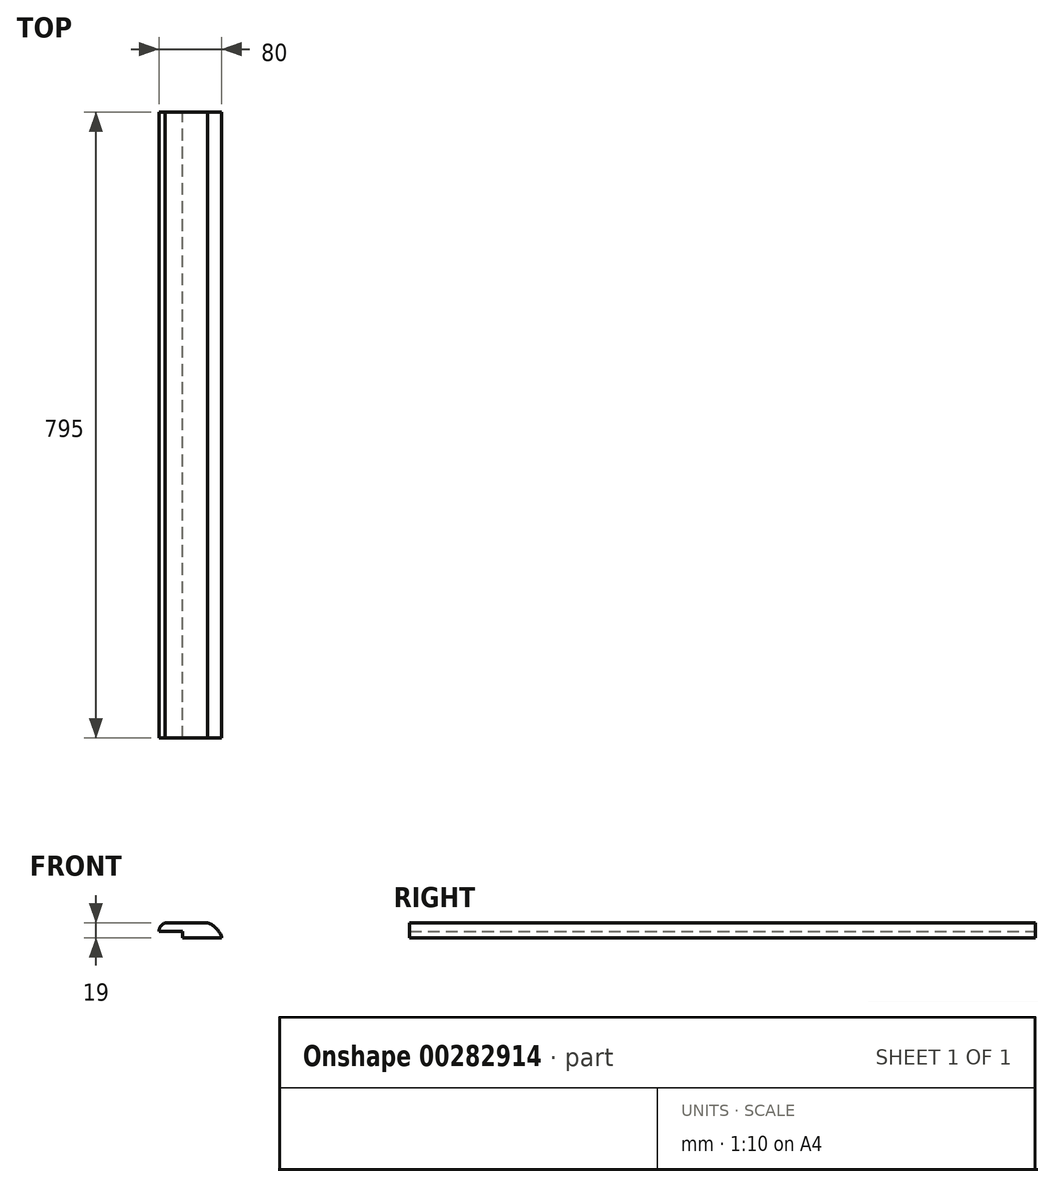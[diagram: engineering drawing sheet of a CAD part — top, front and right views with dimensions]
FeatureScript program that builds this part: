
annotation { "Feature Type Name" : "Feature", "Feature Type Description" : "" }
export const myFeature = defineFeature(function(context is Context, id is Id, definition is map)
    precondition{}
    {
        {
            var Q0;
            Q0=qCreatedBy(makeId("Front.planeOp"),FACE);
            var sketch = newSketch(context, id + "F0", { "sketchPlane" : qUnion([Q0])});
            skLineSegment(sketch, "E0", {"start": v(-32.07, -9.84) * mm, "end": v(-2.07, -9.84) * mm});
            skLineSegment(sketch, "E1", {"start": v(-2.07, -9.84) * mm, "end": v(-2.07, -17.84) * mm});
            skLineSegment(sketch, "E2", {"start": v(-2.07, -17.84) * mm, "end": v(47.93, -17.84) * mm});
            skArc(sketch, "E3", {"start": v(47.93, -17.84) * mm, "mid": v(41.25, -6.14) * mm, "end": v(29.93, 1.16) * mm});
            skLineSegment(sketch, "E4", {"start": v(-24.07, 1.16) * mm, "end": v(29.93, 1.16) * mm});
            skArc(sketch, "E5", {"start": v(-24.07, 1.16) * mm, "mid": v(-29.78, -3.1) * mm, "end": v(-32.07, -9.84) * mm});
            skSolve(sketch);
        }
        {
            var Q0;
            Q0=makeQuery(id+"F0.imprint","IMPRINT",FACE,{"disambiguationData":[TD([[makeQuery(id+"F0.imprint","IMPRINT",EDGE,{"derivedFrom":sQuery(id+"F0.wireOp",EDGE,"E0")}),1.0]])]});
            extrude(context, id + "F1", {"entities" : qUnion([Q0]), "depth" : 795 * mm});
        }
    });
